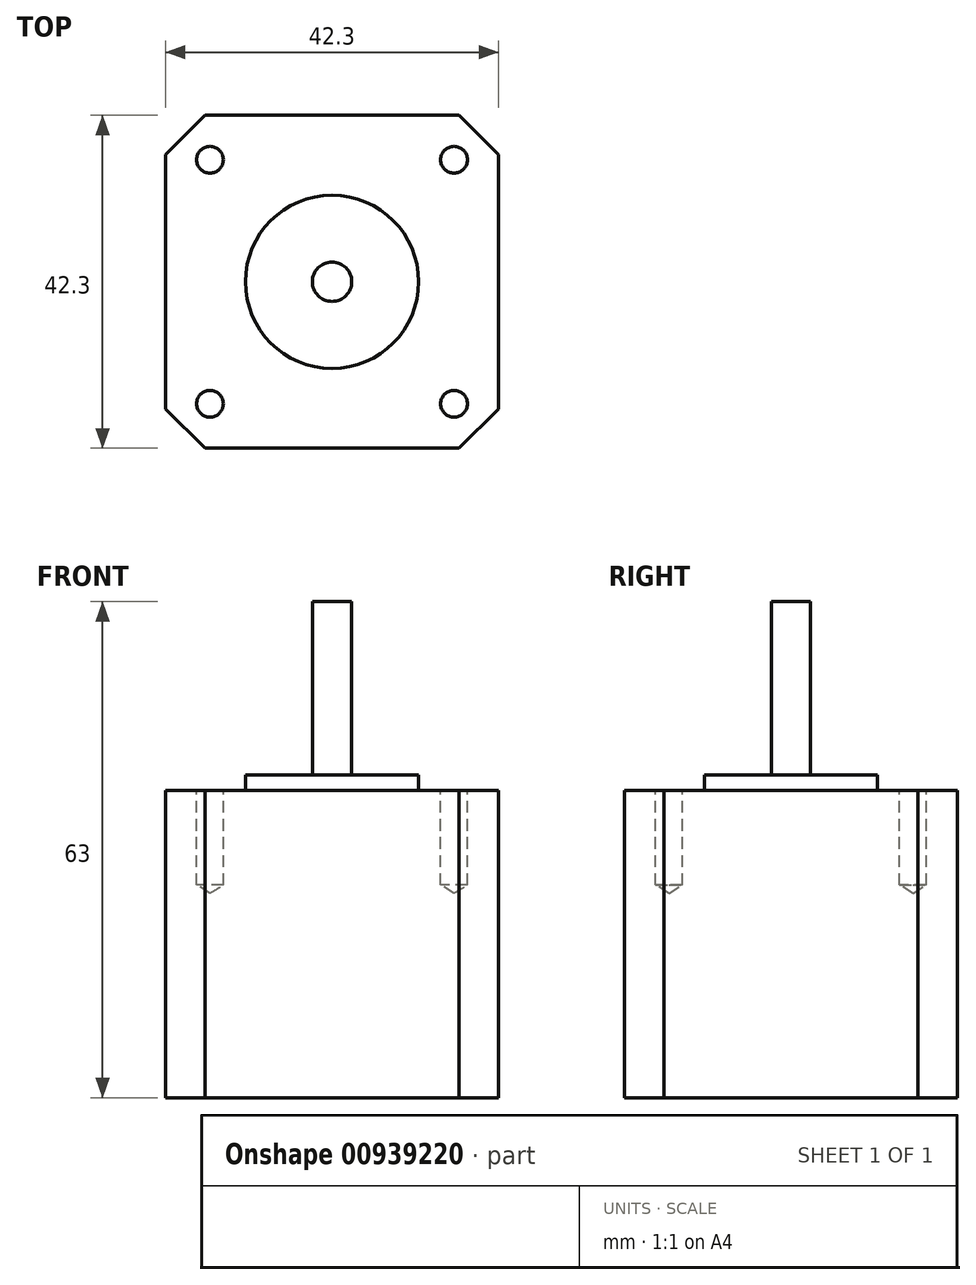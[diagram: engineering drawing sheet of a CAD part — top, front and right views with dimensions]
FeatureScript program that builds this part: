
annotation { "Feature Type Name" : "Feature", "Feature Type Description" : "" }
export const myFeature = defineFeature(function(context is Context, id is Id, definition is map)
    precondition{}
    {
        {
            var Q0;
            Q0=qCreatedBy(makeId("Top.planeOp"),FACE);
            var sketch = newSketch(context, id + "F0", { "sketchPlane" : qUnion([Q0])});
            skLineSegment(sketch, "E0.bottom", {"start": v(21.15, -21.15) * mm, "end": v(-21.15, -21.15) * mm});
            skLineSegment(sketch, "E0.top", {"start": v(21.15, 21.15) * mm, "end": v(-21.15, 21.15) * mm});
            skLineSegment(sketch, "E0.left", {"start": v(21.15, -21.15) * mm, "end": v(21.15, 21.15) * mm});
            skLineSegment(sketch, "E0.right", {"start": v(-21.15, -21.15) * mm, "end": v(-21.15, 21.15) * mm});
            skPoint(sketch, "E0.middle", {"position": v(0, 0) * mm});
            skSolve(sketch);
        }
        {
            var Q0;
            Q0=makeQuery(id+"F0.imprint","IMPRINT",FACE,{"disambiguationData":[TD([[makeQuery(id+"F0.imprint","IMPRINT",EDGE,{"derivedFrom":sQuery(id+"F0.wireOp",EDGE,"E0.bottom")}),-1.0]])]});
            extrude(context, id + "F1", {"entities" : qUnion([Q0]), "oppositeDirection" : true, "depth" : 39 * mm, "offsetDistance" : 25 * mm});
        }
        {
            var Q0;
            Q0=makeQuery(id+"F1.opExtrude","CAP_FACE",FACE,{"disambiguationData":[OSD([sQuery(id+"F0.wireOp",EDGE,"E0.bottom"),sQuery(id+"F0.wireOp",EDGE,"E0.top"),sQuery(id+"F0.wireOp",EDGE,"E0.left"),sQuery(id+"F0.wireOp",EDGE,"E0.right")])],"isStart":true});
            var sketch = newSketch(context, id + "F2", { "sketchPlane" : qUnion([Q0])});
            skCircle(sketch, "E1", {"center": v(0, 0) * mm, "radius": 2.5 * mm});
            skCircle(sketch, "E2", {"center": v(0, 0) * mm, "radius": 11 * mm});
            skLineSegment(sketch, "E3.bottom", {"start": v(15.5, -15.5) * mm, "end": v(-15.5, -15.5) * mm, "construction": true});
            skLineSegment(sketch, "E3.top", {"start": v(15.5, 15.5) * mm, "end": v(-15.5, 15.5) * mm, "construction": true});
            skLineSegment(sketch, "E3.left", {"start": v(15.5, -15.5) * mm, "end": v(15.5, 15.5) * mm, "construction": true});
            skLineSegment(sketch, "E3.right", {"start": v(-15.5, -15.5) * mm, "end": v(-15.5, 15.5) * mm, "construction": true});
            skSolve(sketch);
        }
        {
            var Q0;
            Q0=makeQuery(id+"F2.imprint","IMPRINT",FACE,{"disambiguationData":[TD([[makeQuery(id+"F2.imprint","IMPRINT",EDGE,{"derivedFrom":sQuery(id+"F2.wireOp",EDGE,"E1")}),1.0]])]});
            extrude(context, id + "F3", {"entities" : qUnion([Q0]), "depth" : 24 * mm, "offsetDistance" : 25 * mm});
        }
        {
            var Q0;
            Q0=makeQuery(id+"F2.imprint","IMPRINT",FACE,{"disambiguationData":[TD([[makeQuery(id+"F2.imprint","IMPRINT",EDGE,{"derivedFrom":sQuery(id+"F2.wireOp",EDGE,"E1")}),-1.0]])]});
            extrude(context, id + "F4", {"entities" : qUnion([Q0]), "operationType" : NewBodyOperationType.ADD, "depth" : 2 * mm, "offsetDistance" : 25 * mm});
        }
        {
            var Q0;
            Q0=sQuery(id+"F2.wireOp",VERTEX,"E3.bottom.start");
            var Q1;
            Q1=sQuery(id+"F2.wireOp",VERTEX,"E3.top.start");
            var Q2;
            Q2=sQuery(id+"F2.wireOp",VERTEX,"E3.right.start");
            var Q3;
            Q3=sQuery(id+"F2.wireOp",VERTEX,"E3.right.end");
            var Q4;
            Q4=makeQuery(id+"F1.opExtrude","SWEPT_BODY",BODY,{"disambiguationData":[OSD([sQuery(id+"F0.wireOp",EDGE,"E0.bottom"),sQuery(id+"F0.wireOp",EDGE,"E0.top"),sQuery(id+"F0.wireOp",EDGE,"E0.left"),sQuery(id+"F0.wireOp",EDGE,"E0.right")])]});
            hole(context, id + "F5", {"style" : HoleStyle.SIMPLE, "endStyle" : HoleEndStyle.BLIND, "standardTappedOrClearance" : lookupTablePath({ "standard" : "ISO", "fit" : "Normal", "size" : "M3", "type" : "Clearance" }), "standardBlindInLast" : lookupTablePath({ "fit" : "Normal", "standard" : "ISO", "engagement" : "75%", "pitch" : "0.5 mm", "size" : "M3", "type" : "Clearance & tapped" }), "holeDiameter" : 3.4 * mm, "majorDiameter" : 5 * mm, "holeDepth" : 12 * mm, "isTappedThrough" : true, "tappedDepth" : 12 * mm, "tapClearance" : 3, "locations" : qUnion([Q0, Q1, Q2, Q3]), "scope" : qUnion([Q4])});
        }
        {
            var Q0;
            Q0=makeQuery(id+"F1.opExtrude","SWEPT_EDGE",EDGE,{"disambiguationData":[OSD([sQuery(id+"F0.wireOp",EDGE,"E0.bottom"),sQuery(id+"F0.wireOp",EDGE,"E0.right")])]});
            var Q1;
            Q1=makeQuery(id+"F1.opExtrude","SWEPT_EDGE",EDGE,{"disambiguationData":[OSD([sQuery(id+"F0.wireOp",EDGE,"E0.top"),sQuery(id+"F0.wireOp",EDGE,"E0.left")])]});
            var Q2;
            Q2=makeQuery(id+"F1.opExtrude","SWEPT_EDGE",EDGE,{"disambiguationData":[OSD([sQuery(id+"F0.wireOp",EDGE,"E0.bottom"),sQuery(id+"F0.wireOp",EDGE,"E0.left")])]});
            var Q3;
            Q3=makeQuery(id+"F1.opExtrude","SWEPT_EDGE",EDGE,{"disambiguationData":[OSD([sQuery(id+"F0.wireOp",EDGE,"E0.top"),sQuery(id+"F0.wireOp",EDGE,"E0.right")])]});
            chamfer(context, id + "F6", {"entities" : qUnion([Q0, Q1, Q2, Q3]), "width" : 5 * mm, "tangentPropagation" : true});
        }
    });
